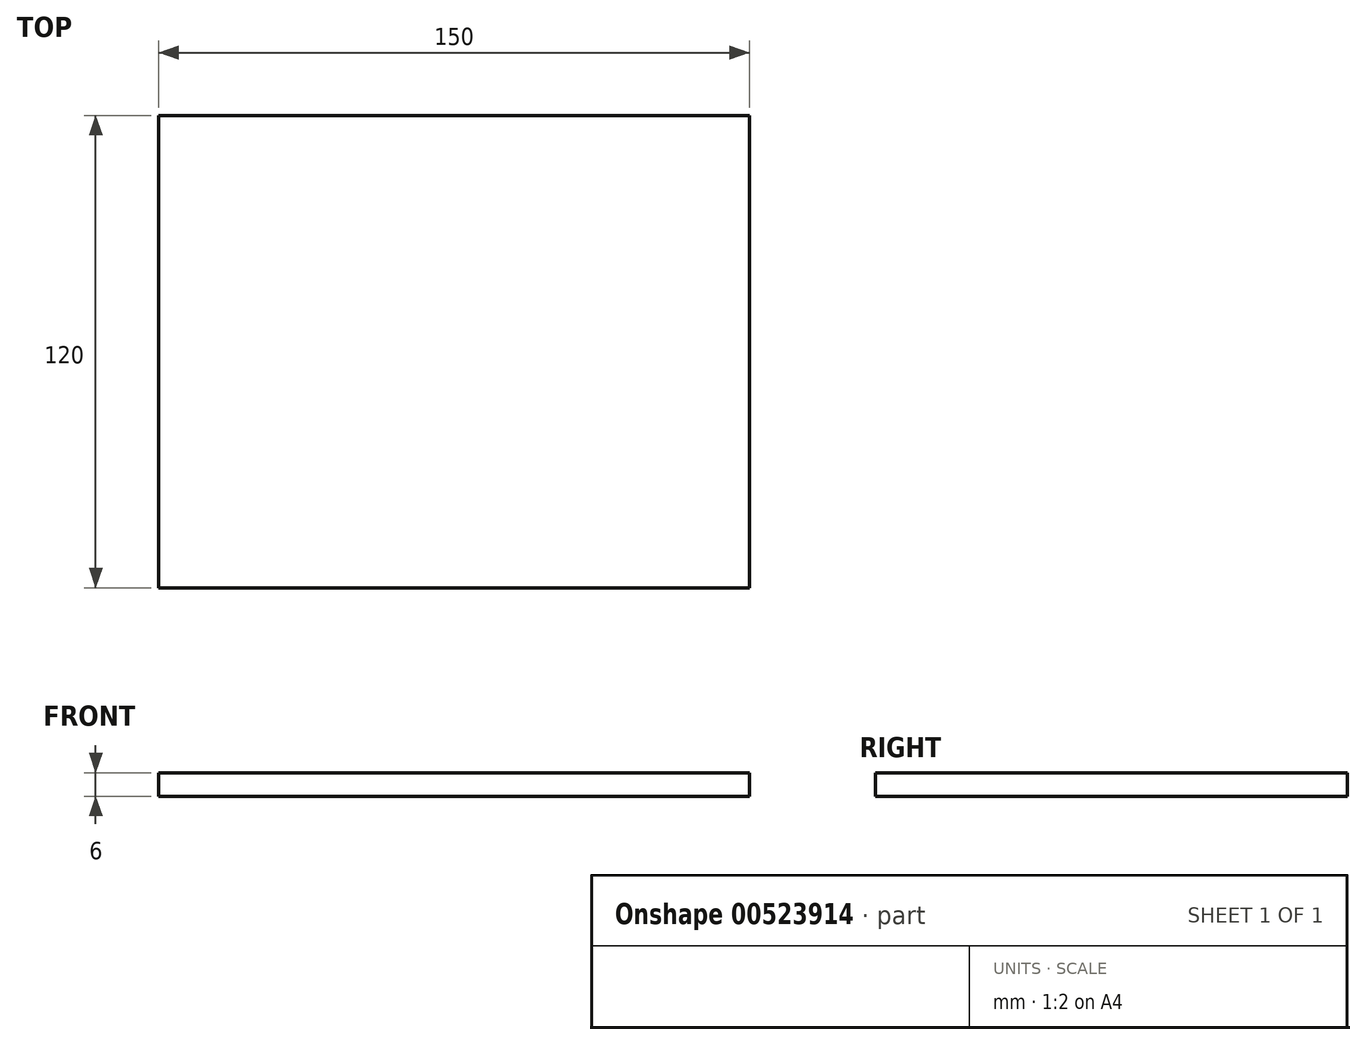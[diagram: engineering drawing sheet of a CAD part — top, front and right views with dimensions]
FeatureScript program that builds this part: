
annotation { "Feature Type Name" : "Feature", "Feature Type Description" : "" }
export const myFeature = defineFeature(function(context is Context, id is Id, definition is map)
    precondition{}
    {
        {
            var Q0;
            Q0=qCreatedBy(makeId("Top.planeOp"),FACE);
            var sketch = newSketch(context, id + "F0", { "sketchPlane" : qUnion([Q0])});
            skLineSegment(sketch, "E0.bottom", {"start": v(75, 60) * mm, "end": v(-75, 60) * mm});
            skLineSegment(sketch, "E0.top", {"start": v(75, -60) * mm, "end": v(-75, -60) * mm});
            skLineSegment(sketch, "E0.left", {"start": v(75, 60) * mm, "end": v(75, -60) * mm});
            skLineSegment(sketch, "E0.right", {"start": v(-75, 60) * mm, "end": v(-75, -60) * mm});
            skPoint(sketch, "E0.middle", {"position": v(0, 0) * mm});
            skSolve(sketch);
        }
        {
            var Q0;
            Q0 = qSketchRegion(id + "F0", true);
            extrude(context, id + "F1", {"entities" : qUnion([Q0]), "depth" : 6 * mm, "offsetDistance" : 25 * mm});
        }
    });
